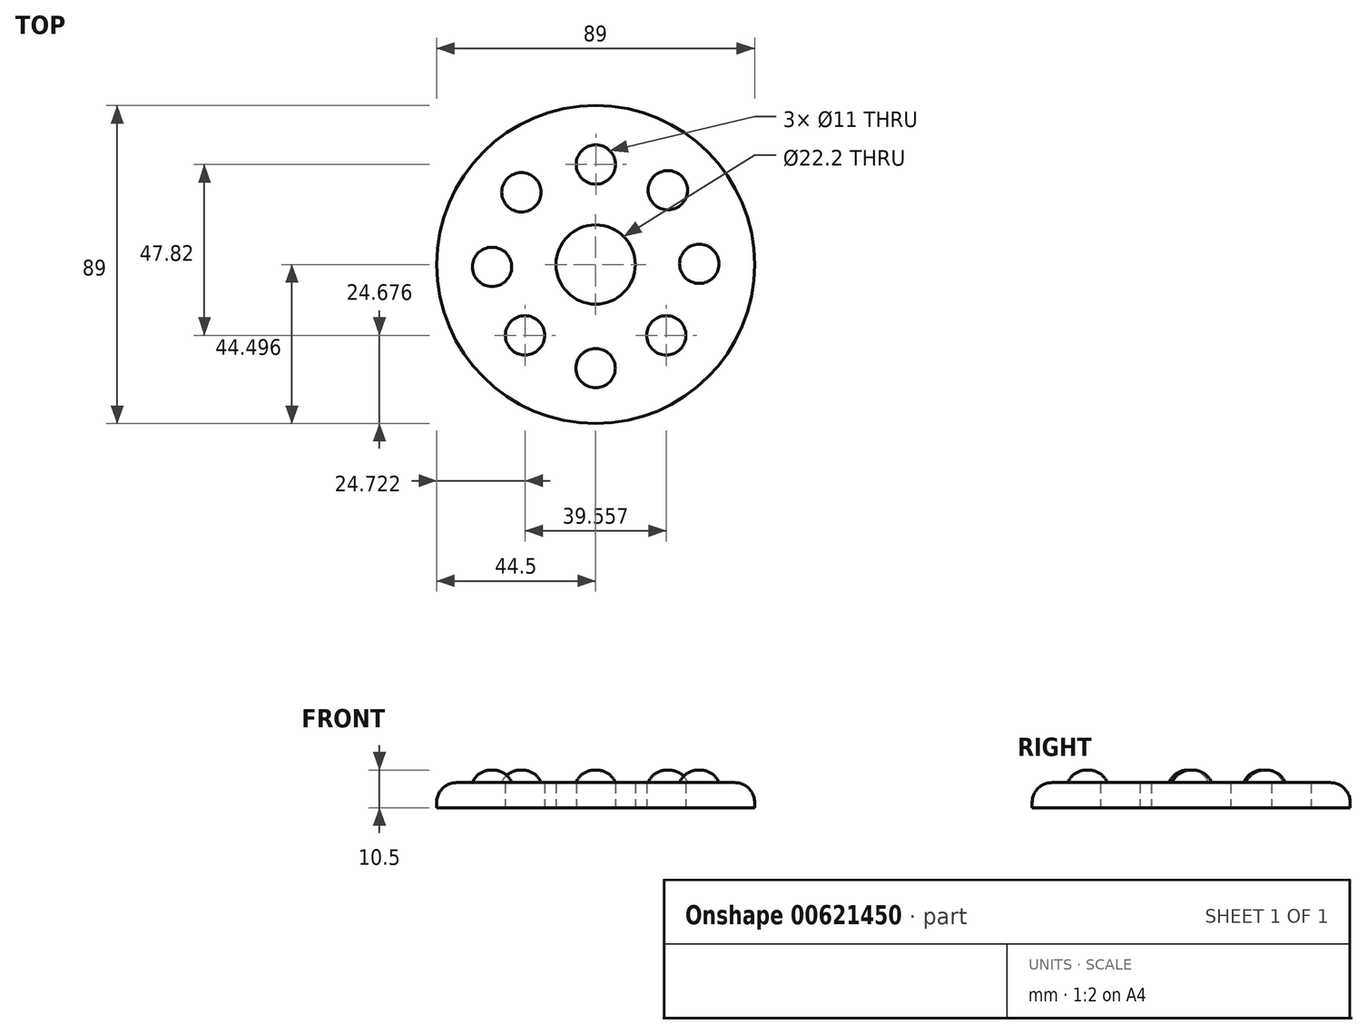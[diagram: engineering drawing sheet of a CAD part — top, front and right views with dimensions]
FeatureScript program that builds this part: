
annotation { "Feature Type Name" : "Feature", "Feature Type Description" : "" }
export const myFeature = defineFeature(function(context is Context, id is Id, definition is map)
    precondition{}
    {
        {
            var Q0;
            Q0=qCreatedBy(makeId("Top.planeOp"),FACE);
            var sketch = newSketch(context, id + "F0", { "sketchPlane" : qUnion([Q0])});
            skCircle(sketch, "E0", {"center": v(0, 0.1) * mm, "radius": 11.1 * mm});
            skCircle(sketch, "E1", {"center": v(0, 0.1) * mm, "radius": 44.5 * mm});
            skLineSegment(sketch, "E2", {"start": v(-44.5, 0.1) * mm, "end": v(44.5, 0.1) * mm, "construction": true});
            skLineSegment(sketch, "E3", {"start": v(0.06, 44.6) * mm, "end": v(0.06, -44.4) * mm, "construction": true});
            skPoint(sketch, "E4", {"position": v(39.5, 0.1) * mm});
            skPoint(sketch, "E5", {"position": v(0.06, 39.46) * mm});
            skPoint(sketch, "E6", {"position": v(-39.61, 0.1) * mm});
            skPoint(sketch, "E7", {"position": v(0.06, -39.54) * mm});
            skLineSegment(sketch, "E8", {"start": v(-39.61, 0.1) * mm, "end": v(0.06, 39.46) * mm, "construction": true});
            skLineSegment(sketch, "E9", {"start": v(0.06, 39.46) * mm, "end": v(39.5, 0.1) * mm, "construction": true});
            skLineSegment(sketch, "E10", {"start": v(39.5, 0.1) * mm, "end": v(0.06, -39.54) * mm, "construction": true});
            skLineSegment(sketch, "E11", {"start": v(0.06, -39.54) * mm, "end": v(-39.61, 0.1) * mm, "construction": true});
            skLineSegment(sketch, "E12", {"start": v(-19.78, 19.78) * mm, "end": v(-31.47, 31.56) * mm, "construction": true});
            skLineSegment(sketch, "E13", {"start": v(-19.78, 19.78) * mm, "end": v(19.78, -19.72) * mm, "construction": true});
            skLineSegment(sketch, "E14", {"start": v(19.78, -19.72) * mm, "end": v(31.4, -31.44) * mm, "construction": true});
            skLineSegment(sketch, "E15", {"start": v(-19.78, -19.72) * mm, "end": v(-31.44, -31.4) * mm, "construction": true});
            skLineSegment(sketch, "E16", {"start": v(-19.78, -19.72) * mm, "end": v(19.78, 19.78) * mm, "construction": true});
            skLineSegment(sketch, "E17", {"start": v(19.78, 19.78) * mm, "end": v(31.5, 31.53) * mm, "construction": true});
            skCircle(sketch, "E18", {"center": v(-19.78, -19.72) * mm, "radius": 5.5 * mm});
            skCircle(sketch, "E19", {"center": v(19.78, -19.72) * mm, "radius": 5.5 * mm});
            skCircle(sketch, "E20", {"center": v(0.06, 28.1) * mm, "radius": 5.5 * mm});
            skLineSegment(sketch, "E21", {"start": v(-19.78, 19.78) * mm, "end": v(19.78, 19.78) * mm, "construction": true});
            skLineSegment(sketch, "E22", {"start": v(19.78, -19.72) * mm, "end": v(19.78, 19.78) * mm, "construction": true});
            skLineSegment(sketch, "E23", {"start": v(19.78, -19.72) * mm, "end": v(-19.78, -19.72) * mm, "construction": true});
            skLineSegment(sketch, "E24", {"start": v(-19.78, 19.78) * mm, "end": v(-19.78, -19.72) * mm, "construction": true});
            skSolve(sketch);
        }
        {
            var Q0;
            Q0 = qSketchRegion(id + "F0", true);
            extrude(context, id + "F1", {"entities" : qUnion([Q0]), "depth" : 7 * mm, "offsetDistance" : 25 * mm});
        }
        {
            var Q0;
            Q0=makeQuery(id+"F1.opExtrude","CAP_EDGE",EDGE,{"disambiguationData":[OSD([sQuery(id+"F0.wireOp",EDGE,"E1")])],"isStart":false});
            fillet(context, id + "F2", {"entities" : qUnion([Q0]), "radius" : 5.55 * mm, "tangentPropagation" : true, "allowEdgeOverflow" : false});
        }
        {
            var Q0;
            Q0=makeQuery(id+"F1.opExtrude","CAP_FACE",FACE,{"disambiguationData":[OSD([sQuery(id+"F0.wireOp",EDGE,"E0"),sQuery(id+"F0.wireOp",EDGE,"E1"),sQuery(id+"F0.wireOp",EDGE,"E18"),sQuery(id+"F0.wireOp",EDGE,"E19"),sQuery(id+"F0.wireOp",EDGE,"E20")])],"isStart":false});
            var sketch = newSketch(context, id + "F3", { "sketchPlane" : qUnion([Q0])});
            skCircle(sketch, "E25", {"center": v(20.2, 20.9) * mm, "radius": 5.5 * mm});
            skCircle(sketch, "E26", {"center": v(29, 0.3) * mm, "radius": 5.5 * mm});
            skCircle(sketch, "E27", {"center": v(0, -28.9) * mm, "radius": 5.5 * mm});
            skCircle(sketch, "E28", {"center": v(-29, -0.56) * mm, "radius": 5.5 * mm});
            skCircle(sketch, "E29", {"center": v(-20.79, 20.32) * mm, "radius": 5.5 * mm});
            skSolve(sketch);
        }
        {
            var Q0;
            Q0 = qSketchRegion(id + "F3", true);
            extrude(context, id + "F4", {"entities" : qUnion([Q0]), "operationType" : NewBodyOperationType.ADD, "depth" : 3.5 * mm, "offsetDistance" : 25 * mm});
        }
        {
            var Q0;
            Q0=makeQuery(id+"F4.opExtrude","CAP_EDGE",EDGE,{"disambiguationData":[OSD([sQuery(id+"F3.wireOp",EDGE,"E28")])],"isStart":false});
            var Q1;
            Q1=makeQuery(id+"F4.opExtrude","CAP_EDGE",EDGE,{"disambiguationData":[OSD([sQuery(id+"F3.wireOp",EDGE,"E29")])],"isStart":false});
            var Q2;
            Q2=makeQuery(id+"F4.opExtrude","CAP_EDGE",EDGE,{"disambiguationData":[OSD([sQuery(id+"F3.wireOp",EDGE,"E25")])],"isStart":false});
            var Q3;
            Q3=makeQuery(id+"F4.opExtrude","CAP_EDGE",EDGE,{"disambiguationData":[OSD([sQuery(id+"F3.wireOp",EDGE,"E26")])],"isStart":false});
            var Q4;
            Q4=makeQuery(id+"F4.opExtrude","CAP_EDGE",EDGE,{"disambiguationData":[OSD([sQuery(id+"F3.wireOp",EDGE,"E27")])],"isStart":false});
            fillet(context, id + "F5", {"entities" : qUnion([Q0, Q1, Q2, Q3, Q4]), "radius" : 5.5 * mm, "tangentPropagation" : true, "allowEdgeOverflow" : false});
        }
    });
